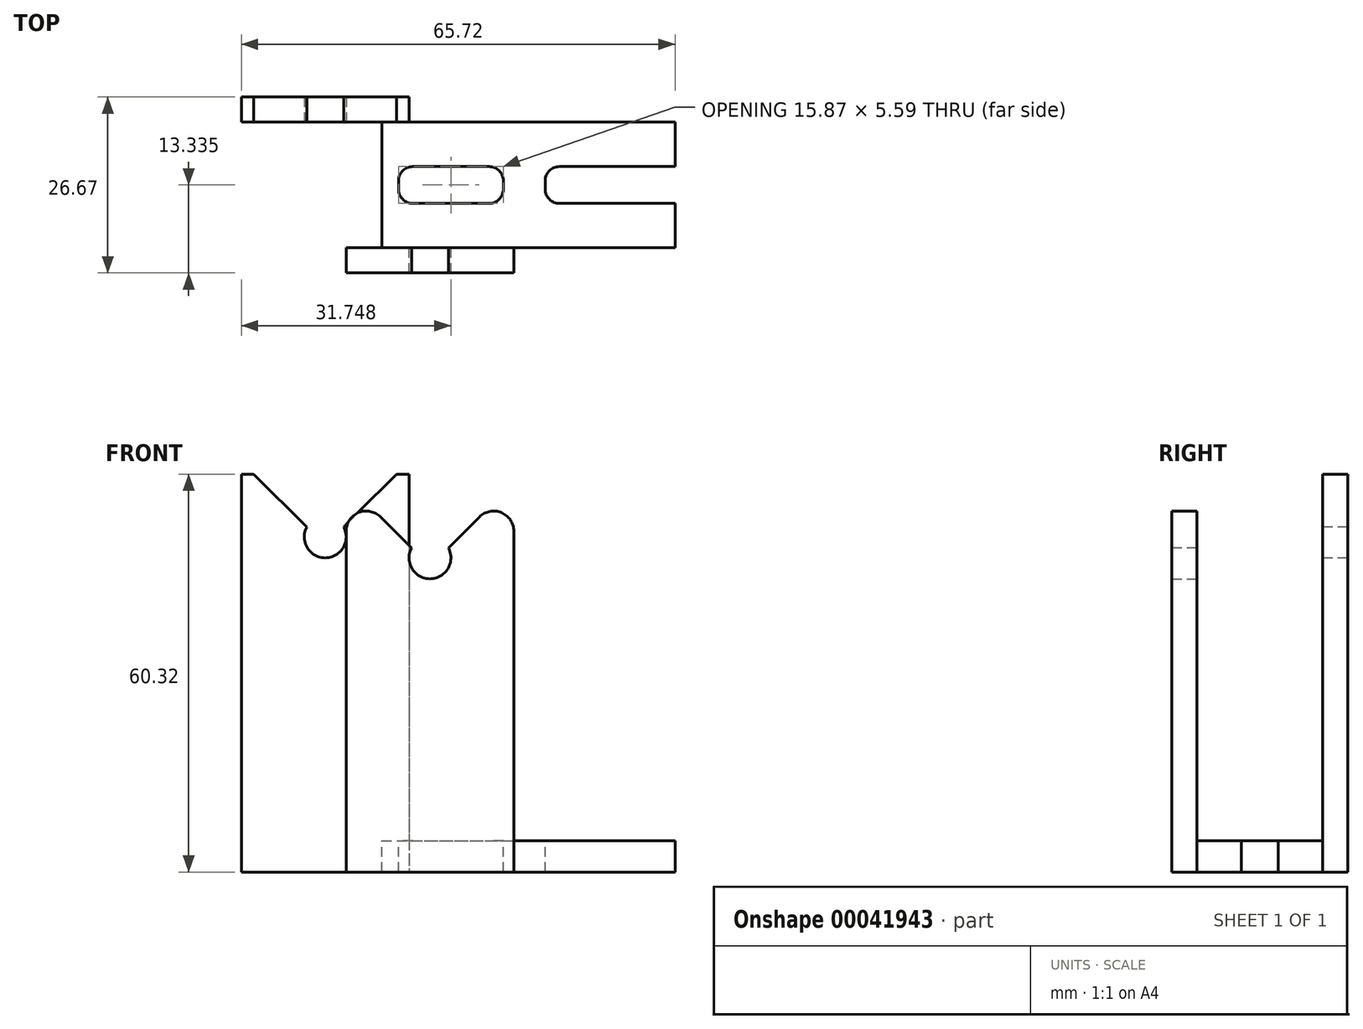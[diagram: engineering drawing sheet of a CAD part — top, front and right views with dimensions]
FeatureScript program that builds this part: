
annotation { "Feature Type Name" : "Feature", "Feature Type Description" : "" }
export const myFeature = defineFeature(function(context is Context, id is Id, definition is map)
    precondition{}
    {
        {
            var Q0;
            Q0=qCreatedBy(makeId("Front.planeOp"),FACE);
            var sketch = newSketch(context, id + "F0", { "sketchPlane" : qUnion([Q0])});
            skLineSegment(sketch, "E0", {"start": v(0, -85.73) * mm, "end": v(-44.45, -85.73) * mm});
            skLineSegment(sketch, "E1", {"start": v(-44.45, -85.73) * mm, "end": v(-44.45, -80.96) * mm});
            skLineSegment(sketch, "E2", {"start": v(-44.45, -80.96) * mm, "end": v(0, -80.96) * mm});
            skLineSegment(sketch, "E3", {"start": v(0, -80.96) * mm, "end": v(0, -85.73) * mm});
            skLineSegment(sketch, "E4", {"start": v(0, 0) * mm, "end": v(43.58, 0) * mm, "construction": true});
            skPoint(sketch, "E5", {"position": v(-10.48, -85.73) * mm});
            skPoint(sketch, "E6", {"position": v(-32.7, -85.73) * mm});
            skSolve(sketch);
        }
        {
            var Q0;
            Q0=qSketchRegion(id+"F0",true);
            extrude(context, id + "F1", {"entities" : qUnion([Q0]), "depth" : 19.05 * mm});
        }
        {
            var Q0;
            Q0=makeQuery(id+"F1.opExtrude","SWEPT_FACE",FACE,{"disambiguationData":[OSD([sQuery(id+"F0.wireOp",EDGE,"E2")])]});
            var sketch = newSketch(context, id + "F2", { "sketchPlane" : qUnion([Q0])});
            skLineSegment(sketch, "E7.bottom", {"start": v(-41.9, -6.73) * mm, "end": v(-26.03, -6.73) * mm});
            skLineSegment(sketch, "E7.top", {"start": v(-41.9, -12.32) * mm, "end": v(-26.03, -12.32) * mm});
            skLineSegment(sketch, "E7.left", {"start": v(-41.9, -6.73) * mm, "end": v(-41.9, -12.32) * mm});
            skLineSegment(sketch, "E7.right", {"start": v(-26.03, -6.73) * mm, "end": v(-26.03, -12.32) * mm});
            skLineSegment(sketch, "E8.bottom", {"start": v(-19.68, -6.73) * mm, "end": v(-3.8, -6.73) * mm});
            skLineSegment(sketch, "E8.top", {"start": v(-19.68, -12.32) * mm, "end": v(-3.8, -12.32) * mm});
            skLineSegment(sketch, "E8.left", {"start": v(-19.68, -6.73) * mm, "end": v(-19.68, -12.32) * mm});
            skLineSegment(sketch, "E8.right", {"start": v(-3.8, -6.73) * mm, "end": v(-3.8, -12.32) * mm});
            skPoint(sketch, "E9", {"position": v(-33.97, -6.73) * mm});
            skLineSegment(sketch, "E10", {"start": v(-3.8, -9.53) * mm, "end": v(0, -9.53) * mm, "construction": true});
            skSolve(sketch);
        }
        {
            var Q0;
            Q0=qSketchRegion(id+"F2",true);
            extrude(context, id + "F3", {"entities" : qUnion([Q0]), "operationType" : NewBodyOperationType.REMOVE, "endBound" : BoundingType.THROUGH_ALL, "oppositeDirection" : true, "depth" : 25.4 * mm});
        }
        {
            var Q0;
            Q0=makeQuery(id+"F3.boolean.opBoolean","COPY",EDGE,{"derivedFrom":makeQuery(id+"F3.opExtrude","SWEPT_EDGE",EDGE,{"disambiguationData":[OSD([sQuery(id+"F2.wireOp",EDGE,"E8.bottom"),sQuery(id+"F2.wireOp",EDGE,"E8.right")])]})});
            var Q1;
            Q1=makeQuery(id+"F3.boolean.opBoolean","COPY",EDGE,{"derivedFrom":makeQuery(id+"F3.opExtrude","SWEPT_EDGE",EDGE,{"disambiguationData":[OSD([sQuery(id+"F2.wireOp",EDGE,"E7.bottom"),sQuery(id+"F2.wireOp",EDGE,"E7.right")])]})});
            var Q2;
            Q2=makeQuery(id+"F3.boolean.opBoolean","COPY",EDGE,{"derivedFrom":makeQuery(id+"F3.opExtrude","SWEPT_EDGE",EDGE,{"disambiguationData":[OSD([sQuery(id+"F2.wireOp",EDGE,"E8.top"),sQuery(id+"F2.wireOp",EDGE,"E8.right")])]})});
            var Q3;
            Q3=makeQuery(id+"F3.boolean.opBoolean","COPY",EDGE,{"derivedFrom":makeQuery(id+"F3.opExtrude","SWEPT_EDGE",EDGE,{"disambiguationData":[OSD([sQuery(id+"F2.wireOp",EDGE,"E7.top"),sQuery(id+"F2.wireOp",EDGE,"E7.right")])]})});
            var Q4;
            Q4=makeQuery(id+"F3.boolean.opBoolean","COPY",EDGE,{"derivedFrom":makeQuery(id+"F3.opExtrude","SWEPT_EDGE",EDGE,{"disambiguationData":[OSD([sQuery(id+"F2.wireOp",EDGE,"E8.bottom"),sQuery(id+"F2.wireOp",EDGE,"E8.left")])]})});
            var Q5;
            Q5=makeQuery(id+"F3.boolean.opBoolean","COPY",EDGE,{"derivedFrom":makeQuery(id+"F3.opExtrude","SWEPT_EDGE",EDGE,{"disambiguationData":[OSD([sQuery(id+"F2.wireOp",EDGE,"E7.bottom"),sQuery(id+"F2.wireOp",EDGE,"E7.left")])]})});
            var Q6;
            Q6=makeQuery(id+"F3.boolean.opBoolean","COPY",EDGE,{"derivedFrom":makeQuery(id+"F3.opExtrude","SWEPT_EDGE",EDGE,{"disambiguationData":[OSD([sQuery(id+"F2.wireOp",EDGE,"E8.top"),sQuery(id+"F2.wireOp",EDGE,"E8.left")])]})});
            var Q7;
            Q7=makeQuery(id+"F3.boolean.opBoolean","COPY",EDGE,{"derivedFrom":makeQuery(id+"F3.opExtrude","SWEPT_EDGE",EDGE,{"disambiguationData":[OSD([sQuery(id+"F2.wireOp",EDGE,"E7.top"),sQuery(id+"F2.wireOp",EDGE,"E7.left")])]})});
            fillet(context, id + "F4", {"entities" : qUnion([Q0, Q1, Q2, Q3, Q4, Q5, Q6, Q7]), "radius" : 2.16 * mm, "tangentPropagation" : true, "allowEdgeOverflow" : false});
        }
        {
            var Q0;
            Q0=qCreatedBy(makeId("Front.planeOp"),FACE);
            var sketch = newSketch(context, id + "F5", { "sketchPlane" : qUnion([Q0])});
            skLineSegment(sketch, "E11", {"start": v(-44.45, -85.73) * mm, "end": v(0, -85.73) * mm});
            skLineSegment(sketch, "E12", {"start": v(-44.45, -85.73) * mm, "end": v(-65.72, -85.73) * mm});
            skLineSegment(sketch, "E13", {"start": v(-65.72, -85.73) * mm, "end": v(-65.72, -25.4) * mm});
            skLineSegment(sketch, "E14", {"start": v(-65.72, -25.4) * mm, "end": v(-40.32, -25.4) * mm});
            skLineSegment(sketch, "E15", {"start": v(-40.32, -25.4) * mm, "end": v(-40.32, -85.73) * mm});
            skLineSegment(sketch, "E16", {"start": v(-40.32, -85.73) * mm, "end": v(0, -85.73) * mm});
            skCircle(sketch, "E17", {"center": v(-53.02, -34.93) * mm, "radius": 3.18 * mm});
            skPoint(sketch, "E18", {"position": v(-11.75, -85.73) * mm});
            skSolve(sketch);
        }
        {
            var Q0;
            Q0=qSketchRegion(id+"F5",true);
            extrude(context, id + "F6", {"entities" : qUnion([Q0]), "operationType" : NewBodyOperationType.ADD, "oppositeDirection" : true, "depth" : 3.8 * mm});
        }
        {
            var Q0;
            {var subQ0=sQuery(id+"F5.wireOp",EDGE,"E11");Q0=makeQuery(id+"F6OMcOAtScRA9T7_1.boolean.opBoolean","MERGE",FACE,{"derivedFrom":[makeQuery(id+"F6.boolean.opBoolean","MERGE",FACE,{"derivedFrom":[makeQuery(id+"F1.opExtrude","SWEPT_FACE",FACE,{"disambiguationData":[OSD([sQuery(id+"F0.wireOp",EDGE,"E0")])]}),makeQuery(id+"F6.opExtrude","SWEPT_FACE",FACE,{"disambiguationData":[OSD([subQ0])]})]}),makeQuery(id+"F6OMcOAtScRA9T7_1.opExtrude","SWEPT_FACE",FACE,{"disambiguationData":[OSD([subQ0])]})]});}
            var sketch = newSketch(context, id + "F7", { "sketchPlane" : qUnion([Q0])});
            skLineSegment(sketch, "E19.bottom", {"start": v(-10.19, 6.73) * mm, "end": v(24.08, 6.73) * mm});
            skLineSegment(sketch, "E19.top", {"start": v(-10.19, 12.32) * mm, "end": v(24.08, 12.32) * mm});
            skLineSegment(sketch, "E19.left", {"start": v(-10.19, 6.73) * mm, "end": v(-10.19, 12.32) * mm});
            skLineSegment(sketch, "E19.right", {"start": v(24.08, 6.73) * mm, "end": v(24.08, 12.32) * mm});
            skSolve(sketch);
        }
        {
            var Q0;
            Q0 = qSketchRegion(id + "F7", true);
            extrude(context, id + "F8", {"entities" : qUnion([Q0]), "operationType" : NewBodyOperationType.REMOVE, "oppositeDirection" : true, "depth" : 25.4 * mm});
        }
        {
            var Q0;
            Q0=qCreatedBy(makeId("Front.planeOp"),FACE);
            var sketch = newSketch(context, id + "F9", { "sketchPlane" : qUnion([Q0])});
            skLineSegment(sketch, "E20", {"start": v(-53.02, -36.21) * mm, "end": v(-68.92, -20.31) * mm});
            skLineSegment(sketch, "E21", {"start": v(-68.92, -20.31) * mm, "end": v(-37.12, -20.31) * mm});
            skLineSegment(sketch, "E22", {"start": v(-37.12, -20.31) * mm, "end": v(-53.02, -36.21) * mm});
            skLineSegment(sketch, "E23", {"start": v(-55.82, -33.42) * mm, "end": v(-50.23, -33.42) * mm, "construction": true});
            skSolve(sketch);
        }
        {
            var Q0;
            Q0 = qSketchRegion(id + "F9", true);
            extrude(context, id + "F10", {"entities" : qUnion([Q0]), "operationType" : NewBodyOperationType.REMOVE, "endBound" : BoundingType.THROUGH_ALL, "oppositeDirection" : true, "depth" : 25.4 * mm, "hasSecondDirection" : true, "secondDirectionBound" : SecondDirectionBoundingType.THROUGH_ALL, "secondDirectionOppositeDirection" : false, "secondDirectionDepth" : 25.4 * mm});
        }
        {
            var Q0;
            Q0=makeQuery(id+"F1.opExtrude","CAP_FACE",FACE,{"disambiguationData":[OSD([sQuery(id+"F0.wireOp",EDGE,"E0"),sQuery(id+"F0.wireOp",EDGE,"E1"),sQuery(id+"F0.wireOp",EDGE,"E2"),sQuery(id+"F0.wireOp",EDGE,"E3")])],"isStart":false});
            var sketch = newSketch(context, id + "F11", { "sketchPlane" : qUnion([Q0])});
            skLineSegment(sketch, "E24.bottom", {"start": v(-24.45, -85.73) * mm, "end": v(-49.85, -85.73) * mm});
            skLineSegment(sketch, "E24.top", {"start": v(-24.45, -23.87) * mm, "end": v(-49.85, -23.87) * mm});
            skLineSegment(sketch, "E24.left", {"start": v(-24.45, -85.73) * mm, "end": v(-24.45, -23.87) * mm});
            skLineSegment(sketch, "E24.right", {"start": v(-49.85, -85.73) * mm, "end": v(-49.85, -23.87) * mm});
            skCircle(sketch, "E25", {"center": v(-37.15, -38.1) * mm, "radius": 3.18 * mm});
            skPoint(sketch, "E26", {"position": v(-53.02, -34.93) * mm});
            skSolve(sketch);
        }
        {
            var Q0;
            Q0 = qSketchRegion(id + "F11", true);
            extrude(context, id + "F12", {"entities" : qUnion([Q0]), "operationType" : NewBodyOperationType.ADD, "depth" : 3.8 * mm});
        }
        {
            var Q0;
            Q0=makeQuery(id+"F12.opExtrude","CAP_FACE",FACE,{"disambiguationData":[OSD([sQuery(id+"F11.wireOp",EDGE,"E24.bottom"),sQuery(id+"F11.wireOp",EDGE,"E24.top"),sQuery(id+"F11.wireOp",EDGE,"E24.left"),sQuery(id+"F11.wireOp",EDGE,"E24.right"),sQuery(id+"F11.wireOp",EDGE,"E25")])],"isStart":false});
            var sketch = newSketch(context, id + "F13", { "sketchPlane" : qUnion([Q0])});
            skLineSegment(sketch, "E27", {"start": v(-39.94, -36.6) * mm, "end": v(-34.35, -36.6) * mm});
            skLineSegment(sketch, "E28", {"start": v(-39.94, -36.6) * mm, "end": v(-55.1, -21.44) * mm});
            skLineSegment(sketch, "E29", {"start": v(-55.1, -21.44) * mm, "end": v(-19.2, -21.44) * mm});
            skLineSegment(sketch, "E30", {"start": v(-19.2, -21.44) * mm, "end": v(-34.35, -36.6) * mm});
            skSolve(sketch);
        }
        {
            var Q0;
            Q0 = qSketchRegion(id + "F13", true);
            extrude(context, id + "F14", {"entities" : qUnion([Q0]), "operationType" : NewBodyOperationType.REMOVE, "oppositeDirection" : true, "depth" : 5.08 * mm});
        }
        {
            var Q0;
            Q0=makeQuery(id+"F14.boolean.opBoolean","INTERSECT",EDGE,{"derivedFrom":[makeQuery(id+"F12.opExtrude","SWEPT_FACE",FACE,{"disambiguationData":[OSD([sQuery(id+"F11.wireOp",EDGE,"E24.right")])]}),makeQuery(id+"F14.opExtrude","SWEPT_FACE",FACE,{"disambiguationData":[OSD([sQuery(id+"F13.wireOp",EDGE,"E28")])]})]});
            var Q1;
            Q1=makeQuery(id+"F14.boolean.opBoolean","INTERSECT",EDGE,{"derivedFrom":[makeQuery(id+"F12.opExtrude","SWEPT_FACE",FACE,{"disambiguationData":[OSD([sQuery(id+"F11.wireOp",EDGE,"E24.left")])]}),makeQuery(id+"F14.opExtrude","SWEPT_FACE",FACE,{"disambiguationData":[OSD([sQuery(id+"F13.wireOp",EDGE,"E30")])]})]});
            fillet(context, id + "F15", {"entities" : qUnion([Q0, Q1]), "radius" : 3.05 * mm, "tangentPropagation" : true, "allowEdgeOverflow" : false});
        }
    });
